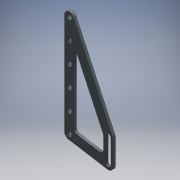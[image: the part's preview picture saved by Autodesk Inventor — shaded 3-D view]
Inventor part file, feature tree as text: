
AUTODESK INVENTOR PART (.ipt)
format: ipt  version: 2016 (Build 200138000, 138)  size: 177,152 bytes
history: native  units: mm
features: fillet x3, extrude x1, sketch x1
ambient origin geometry x8: Origin, YZ Plane, XZ Plane, XY Plane, X Axis, Y Axis, Z Axis, Center Point
bodies: Body1 (feature_tree)
feature tree (5):
  extrude  "Extrusion2"  Depth=6.0mm
  fillet  "Fillet5"  Radius=6.0mm
  fillet  "Fillet6"  Radius=6.0mm
  fillet  "Fillet7"  Radius=6.0mm
  sketch  "Sketch1"  dims[d0=6.0mm d1=6.0mm d2=6.0mm d3=6.0mm d4=6.0mm d5=6.0mm d6=6.0mm d7=25.0mm d8=25.0mm d9=25.0mm d10=25.0mm d11=25.0mm d12=48.0mm d13=8.0mm d14=6.0mm d17=12.0mm d18=12.0mm d20=12.0mm d27=12.0mm d28=12.0mm d29=12.0mm d30=12.0mm d31=30.0mm d32=48.0mm d33=3.0mm d34=0.0mm d35=4.0mm d36=4.0mm d37=4.0mm]
